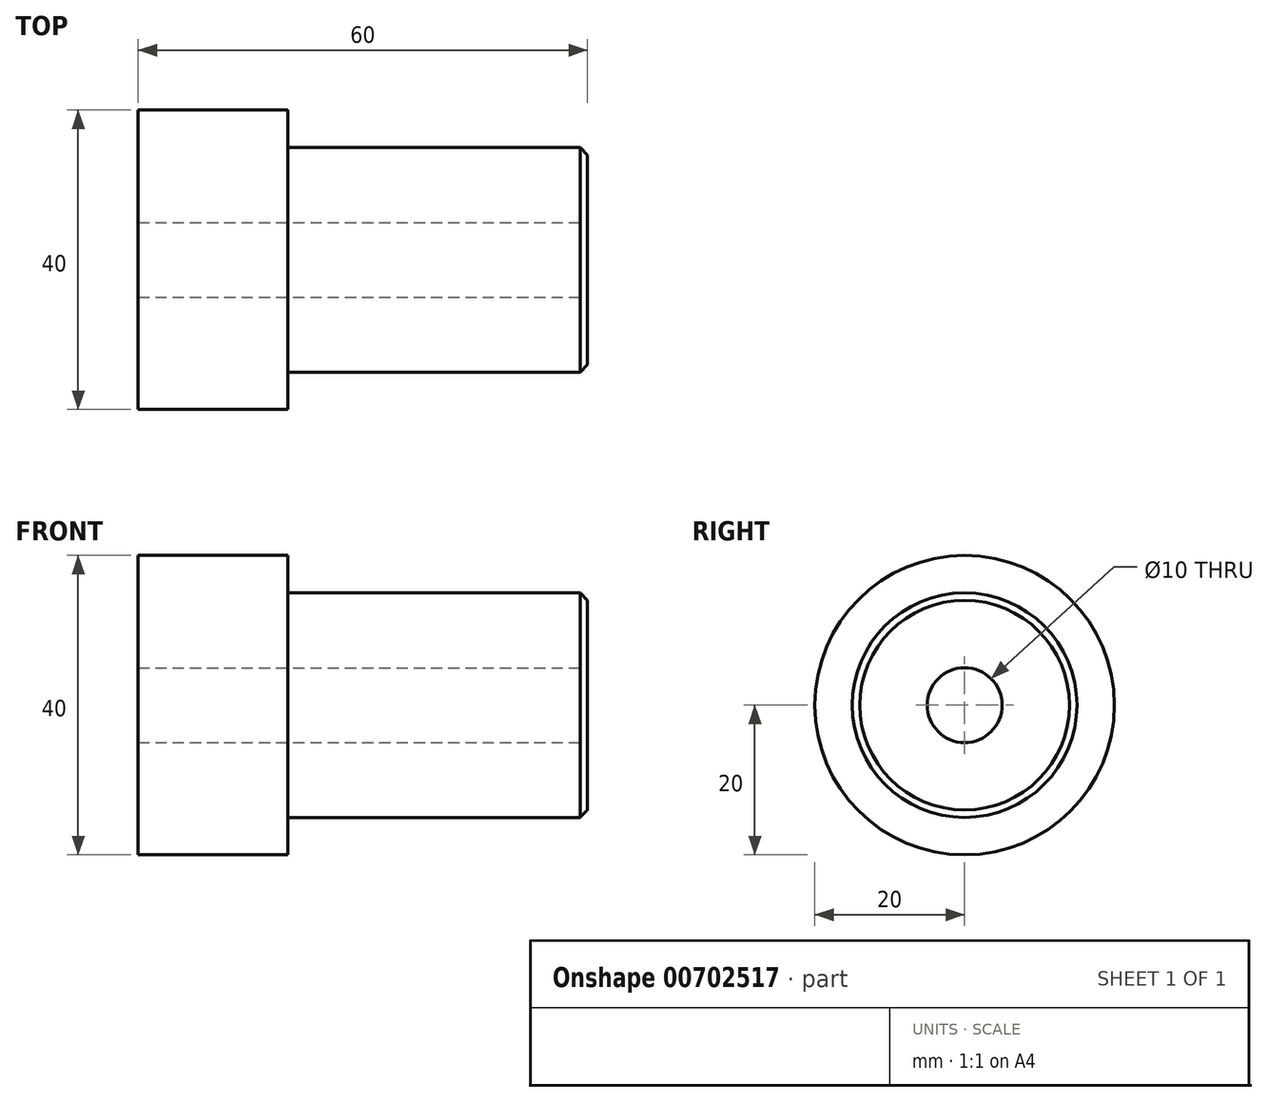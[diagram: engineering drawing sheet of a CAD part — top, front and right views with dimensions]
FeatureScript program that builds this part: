
annotation { "Feature Type Name" : "Feature", "Feature Type Description" : "" }
export const myFeature = defineFeature(function(context is Context, id is Id, definition is map)
    precondition{}
    {
        {
            var Q0;
            Q0=qCreatedBy(makeId("Front.planeOp"),FACE);
            var sketch = newSketch(context, id + "F0", { "sketchPlane" : qUnion([Q0])});
            skLineSegment(sketch, "E0", {"start": v(-45.25, 0) * mm, "end": v(-45.25, 20) * mm});
            skLineSegment(sketch, "E1", {"start": v(-45.25, 20) * mm, "end": v(-25.25, 20) * mm});
            skLineSegment(sketch, "E2", {"start": v(-25.25, 20) * mm, "end": v(-25.25, 15) * mm});
            skLineSegment(sketch, "E3", {"start": v(-25.25, 15) * mm, "end": v(14.75, 15) * mm});
            skLineSegment(sketch, "E4", {"start": v(14.75, 15) * mm, "end": v(14.75, 0) * mm});
            skLineSegment(sketch, "E5", {"start": v(14.75, 0) * mm, "end": v(-45.25, 0) * mm});
            skLineSegment(sketch, "E6", {"start": v(-66.8, 0) * mm, "end": v(38.76, 0) * mm, "construction": true});
            skSolve(sketch);
        }
        {
            var Q0;
            Q0=makeQuery(id+"F0.imprint","IMPRINT",FACE,{"disambiguationData":[TD([[makeQuery(id+"F0.imprint","IMPRINT",EDGE,{"derivedFrom":sQuery(id+"F0.wireOp",EDGE,"E0")}),-1.0]])]});
            var Q1;
            Q1=sQuery(id+"F0.wireOp",EDGE,"E6");
            revolve(context, id + "F1", {"entities" : qUnion([Q0]), "axis" : qUnion([Q1]), "revolveType" : RevolveType.FULL});
        }
        {
            var Q0;
            Q0=makeQuery(id+"F1.opRevolve","SWEPT_FACE",FACE,{"disambiguationData":[OSD([sQuery(id+"F0.wireOp",EDGE,"E4")])]});
            chamfer(context, id + "F2", {"entities" : qUnion([Q0]), "width" : 1 * mm, "tangentPropagation" : true});
        }
        {
            var Q0;
            Q0=makeQuery(id+"F1.opRevolve","SWEPT_FACE",FACE,{"disambiguationData":[OSD([sQuery(id+"F0.wireOp",EDGE,"E4")])]});
            var sketch = newSketch(context, id + "F3", { "sketchPlane" : qUnion([Q0])});
            skCircle(sketch, "E7", {"center": v(0, 0) * mm, "radius": 5 * mm});
            skSolve(sketch);
        }
        {
            var Q0;
            Q0=makeQuery(id+"F3.imprint","IMPRINT",FACE,{"disambiguationData":[TD([[makeQuery(id+"F3.imprint","IMPRINT",EDGE,{"derivedFrom":sQuery(id+"F3.wireOp",EDGE,"E7")}),1.0]])]});
            extrude(context, id + "F4", {"entities" : qUnion([Q0]), "operationType" : NewBodyOperationType.REMOVE, "endBound" : BoundingType.THROUGH_ALL, "oppositeDirection" : true, "depth" : 25 * mm, "offsetDistance" : 25 * mm});
        }
    });
